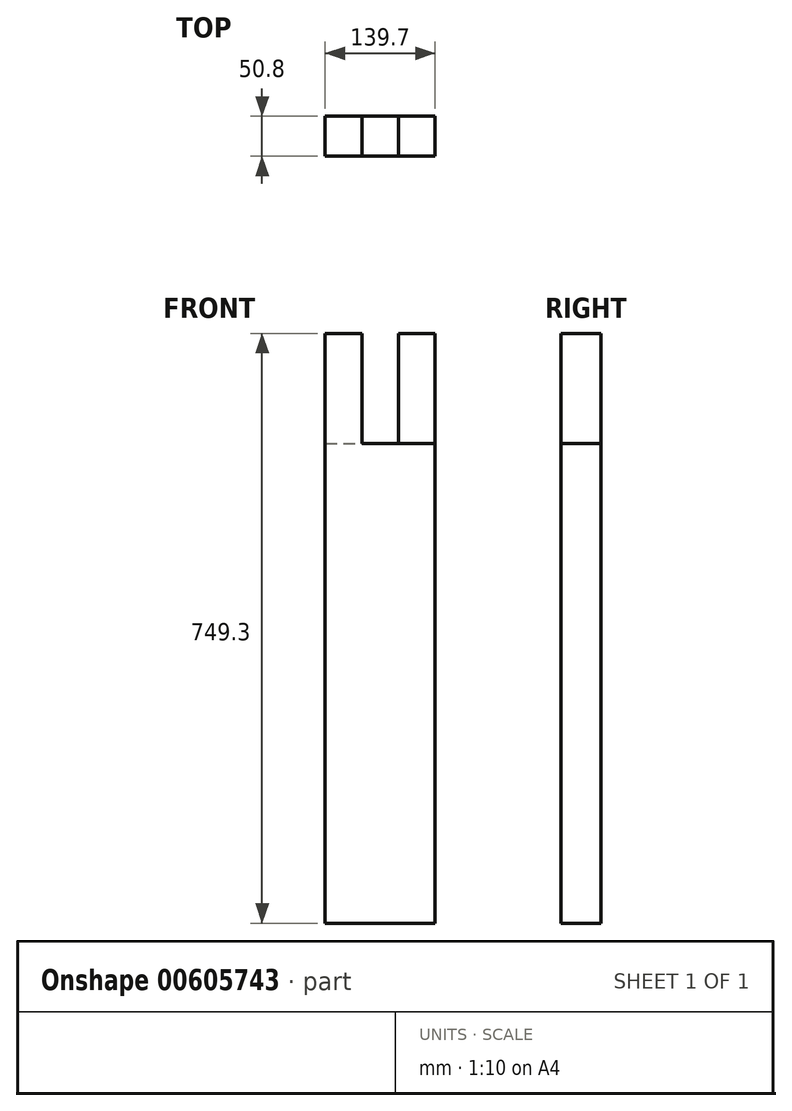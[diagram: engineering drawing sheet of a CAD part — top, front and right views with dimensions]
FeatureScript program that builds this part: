
annotation { "Feature Type Name" : "Feature", "Feature Type Description" : "" }
export const myFeature = defineFeature(function(context is Context, id is Id, definition is map)
    precondition{}
    {
        {
            var Q0;
            Q0=qCreatedBy(makeId("Top.planeOp"),FACE);
            var sketch = newSketch(context, id + "F0", { "sketchPlane" : qUnion([Q0])});
            skLineSegment(sketch, "E0.bottom", {"start": v(-65, 20.08) * mm, "end": v(74.7, 20.08) * mm});
            skLineSegment(sketch, "E0.top", {"start": v(-65, 70.88) * mm, "end": v(74.7, 70.88) * mm});
            skLineSegment(sketch, "E0.left", {"start": v(-65, 20.08) * mm, "end": v(-65, 70.88) * mm});
            skLineSegment(sketch, "E0.right", {"start": v(74.7, 20.08) * mm, "end": v(74.7, 70.88) * mm});
            skPoint(sketch, "E0.middle", {"position": v(4.86, 45.48) * mm});
            skSolve(sketch);
        }
        {
            var Q0;
            Q0=makeQuery(id+"F0.imprint","IMPRINT",FACE,{"disambiguationData":[TD([[makeQuery(id+"F0.imprint","IMPRINT",EDGE,{"derivedFrom":sQuery(id+"F0.wireOp",EDGE,"E0.bottom")}),1.0]])]});
            extrude(context, id + "F1", {"entities" : qUnion([Q0]), "oppositeDirection" : true, "depth" : 609.6 * mm, "offsetDistance" : 25.4 * mm});
        }
        {
            var Q0;
            Q0=makeQuery(id+"F0.imprint","IMPRINT",FACE,{"disambiguationData":[TD([[makeQuery(id+"F0.imprint","IMPRINT",EDGE,{"derivedFrom":sQuery(id+"F0.wireOp",EDGE,"E0.bottom")}),1.0]])]});
            var sketch = newSketch(context, id + "F2", { "sketchPlane" : qUnion([Q0])});
            skLineSegment(sketch, "E1.bottom", {"start": v(-64.94, 20.06) * mm, "end": v(-18.46, 20.06) * mm});
            skLineSegment(sketch, "E1.top", {"start": v(-64.94, 70.86) * mm, "end": v(-18.46, 70.86) * mm});
            skLineSegment(sketch, "E1.left", {"start": v(-64.94, 20.06) * mm, "end": v(-64.94, 70.86) * mm});
            skLineSegment(sketch, "E1.right", {"start": v(-18.46, 20.06) * mm, "end": v(-18.46, 70.86) * mm});
            skSolve(sketch);
        }
        {
            var Q0;
            {var subQ0=sQuery(id+"F2.wireOp",EDGE,"E1.top");Q0=makeQuery(id+"F2.imprint","IMPRINT",FACE,{"disambiguationData":[TD([[makeQuery(id+"F2.imprint","IMPRINT",EDGE,{"derivedFrom":subQ0}),-1.0]])]});}
            extrude(context, id + "F3", {"entities" : qUnion([Q0]), "operationType" : NewBodyOperationType.ADD, "depth" : 139.7 * mm, "offsetDistance" : 25.4 * mm});
        }
        {
            var Q0;
            Q0=makeQuery(id+"F0.imprint","IMPRINT",FACE,{"disambiguationData":[TD([[makeQuery(id+"F0.imprint","IMPRINT",EDGE,{"derivedFrom":sQuery(id+"F0.wireOp",EDGE,"E0.bottom")}),1.0]])]});
            var sketch = newSketch(context, id + "F4", { "sketchPlane" : qUnion([Q0])});
            skLineSegment(sketch, "E2.bottom", {"start": v(74.68, 20.14) * mm, "end": v(28.2, 20.14) * mm});
            skLineSegment(sketch, "E2.top", {"start": v(74.68, 70.94) * mm, "end": v(28.2, 70.94) * mm});
            skLineSegment(sketch, "E2.left", {"start": v(74.68, 20.14) * mm, "end": v(74.68, 70.94) * mm});
            skLineSegment(sketch, "E2.right", {"start": v(28.2, 20.14) * mm, "end": v(28.2, 70.94) * mm});
            skSolve(sketch);
        }
        {
            var Q0;
            {var subQ0=sQuery(id+"F4.wireOp",EDGE,"E2.bottom");Q0=makeQuery(id+"F4.imprint","IMPRINT",FACE,{"disambiguationData":[TD([[makeQuery(id+"F4.imprint","IMPRINT",EDGE,{"derivedFrom":subQ0}),-1.0]])]});}
            extrude(context, id + "F5", {"entities" : qUnion([Q0]), "operationType" : NewBodyOperationType.ADD, "depth" : 139.7 * mm, "offsetDistance" : 25.4 * mm});
        }
    });
